# Revit family: TESK_Насос вертикальный_SVM(T)-45
name_source: partatom
category: Оборудование
units: mm (PartAtom-declared; Revit-internal decimal feet)

## family parameters
Всегда вертикально = Да
Классификация = Насос
На основе рабочей плоскости = Нет
Общий = Нет
При загрузке вырезать с полостями = Нет
Размер круглого соединителя = Использовать диаметр
Тип детали = Вставляется
Точка расчета площади = Нет

## types (50) — shared parameters
ADSK_Версия Revit = 2019
ADSK_Версия семейства = 1.0
ADSK_Диаметр условный = 80 мм
ADSK_Единица измерения = шт.
ADSK_Завод-изготовитель = TESK
ADSK_Классификация нагрузок = Прочее
ADSK_Количество = 1
ADSK_Количество фаз = 3
ADSK_Количество фаз числовое = 3
ADSK_Коэффициент мощности = 1
ADSK_Наименование краткое = Вертикальный многоступенчатый центробежный насос
ADSK_Напряжение = 400 В
URL = www.teskpump.ru
Материал_1 = TESK_Черный_Условный
Материал_2 = TESK_Нержавеющая сталь
Материал_КорпусДвигателя = TESK_Черный_Ребра_Условный
Таблица_Поиска = TESK_SVM(T)-45
УГО_Длина = 365 мм
Фланец_Толщина = 26 мм

## per-type parameters (varying)
| type | ADSK_Код изделия | ADSK_Масса | ADSK_Масса_Текст | ADSK_Наименование | ADSK_Номинальная мощность | ADSK_Полная мощность | D_Башня | Высота_Башня | Высота_Корпуса | Двигатель_Высота | Двигатель_ОтступКоробки | Двигатель_Ширина | Материал_КорпусУлитка | Напор максимальный | Толщина_ФланцаДвигателя |
| SVM 45-1-1 3kW 3x380V 50Hz IE3 | 7745-10-10003380NSSF | 89 | 89 | Вертикальный многоступенчатый центробежный насос SVM, DN80, PN25-40, Hmax=20м (3x380V 50Hz IE3) | 3 кВт | 3 кВ·А | 173 мм | 200 мм | 561 мм | 370 мм | 185 мм | 230 мм | TESK_Нержавеющая сталь | 20 | 11 мм |
| SVM 45-1 4kW 3x380V 50Hz IE3 | 7745-100003380NSSF | 89 | 89 | Вертикальный многоступенчатый центробежный насос SVM, DN80, PN25-40, Hmax=24м (3x380V 50Hz IE3) | 4 кВт | 4 кВ·А | 173 мм | 200 мм | 561 мм | 370 мм | 185 мм | 230 мм | TESK_Нержавеющая сталь | 24 | 11 мм |
| SVM 45-2-2 5.5kW 3x380V 50Hz IE3 | 7745-20-20003380NSSF | 108 | 108 | Вертикальный многоступенчатый центробежный насос SVM, DN80, PN25-40, Hmax=40м (3x380V 50Hz IE3) | 6 кВт | 6 кВ·А | 195 мм | 220 мм | 641 мм | 435 мм | 208 мм | 260 мм | TESK_Нержавеющая сталь | 40 | 13 мм |
| SVM 45-2 7.5kW 3x380V 50Hz IE3 | 7745-20  0003380NSSF | 108 | 108 | Вертикальный многоступенчатый центробежный насос SVM, DN80, PN25-40, Hmax=48м (3x380V 50Hz IE3) | 8 кВт | 8 кВ·А | 195 мм | 220 мм | 641 мм | 435 мм | 208 мм | 260 мм | TESK_Нержавеющая сталь | 48 | 13 мм |
| SVM 45-3-2 11kW 3x380V 50Hz IE3 | 7745-30-20003380NSSF | 183 | 183 | Вертикальный многоступенчатый центробежный насос SVM, DN80, PN25-40, Hmax=63м (3x380V 50Hz IE3) | 11 кВт | 11 кВ·А | 263 мм | 260 мм | 826 мм | 580 мм | 260 мм | 350 мм | TESK_Нержавеющая сталь | 63 | 17 мм |
| SVM 45-3 11kW 3x380V 50Hz IE3 | 7745-300003380NSSF | 183 | 183 | Вертикальный многоступенчатый центробежный насос SVM, DN80, PN25-40, Hmax=71м (3x380V 50Hz IE3) | 11 кВт | 11 кВ·А | 263 мм | 260 мм | 826 мм | 580 мм | 260 мм | 350 мм | TESK_Нержавеющая сталь | 71 | 17 мм |
| SVM 45-4-2 15kW 3x380V 50Hz IE3 | 7745-40-20003380NSSF | 197 | 197 | Вертикальный многоступенчатый центробежный насос SVM, DN80, PN25-40, Hmax=87м (3x380V 50Hz IE3) | 15 кВт | 15 кВ·А | 263 мм | 300 мм | 906 мм | 580 мм | 260 мм | 350 мм | TESK_Нержавеющая сталь | 87 | 17 мм |
| SVM 45-4 15kW 3x380V 50Hz IE3 | 7745-400003380NSSF | 197 | 197 | Вертикальный многоступенчатый центробежный насос SVM, DN80, PN25-40, Hmax=95м (3x380V 50Hz IE3) | 15 кВт | 15 кВ·А | 263 мм | 300 мм | 906 мм | 580 мм | 260 мм | 350 мм | TESK_Нержавеющая сталь | 95 | 17 мм |
| SVM 45-5-2 18.5kW 3x380V 50Hz IE3 | 7745-50-20003380NSSF | 221 | 221 | Вертикальный многоступенчатый центробежный насос SVM, DN80, PN25-40, Hmax=111м (3x380V 50Hz IE3) | 19 кВт | 19 кВ·А | 263 мм | 320 мм | 986 мм | 610 мм | 260 мм | 350 мм | TESK_Нержавеющая сталь | 111 | 18 мм |
| SVM 45-5 18.5kW 3x380V 50Hz IE3 | 7745-500003380NSSF | 221 | 221 | Вертикальный многоступенчатый центробежный насос SVM, DN80, PN25-40, Hmax=119м (3x380V 50Hz IE3) | 19 кВт | 19 кВ·А | 263 мм | 320 мм | 986 мм | 610 мм | 260 мм | 350 мм | TESK_Нержавеющая сталь | 119 | 18 мм |
| SVM 45-6-2 22kW 3x380V 50Hz IE3 | 7745-60-20003380NSSF | 261 | 261 | Вертикальный многоступенчатый центробежный насос SVM, DN80, PN25-40, Hmax=135м (3x380V 50Hz IE3) | 22 кВт | 22 кВ·А | 270 мм | 340 мм | 1066 мм | 645 мм | 285 мм | 360 мм | TESK_Нержавеющая сталь | 135 | 19 мм |
| SVM 45-6 22kW 3x380V 50Hz IE3 | 7745-60   0003380NSSF | 261 | 261 | Вертикальный многоступенчатый центробежный насос SVM, DN80, PN25-40, Hmax=143м (3x380V 50Hz IE3) | 22 кВт | 22 кВ·А | 270 мм | 340 мм | 1066 мм | 645 мм | 285 мм | 360 мм | TESK_Нержавеющая сталь | 143 | 19 мм |
| SVM 45-7-2 30kW 3x380V 50Hz IE3 | 7745-70-20003380NSSF | 320 | 320 | Вертикальный многоступенчатый центробежный насос SVM, DN80, PN25-40, Hmax=158м (3x380V 50Hz IE3) | 30 кВт | 30 кВ·А | 300 мм | 380 мм | 1146 мм | 705 мм | 310 мм | 400 мм | TESK_Нержавеющая сталь | 158 | 21 мм |
| SVM 45-7 30kW 3x380V 50Hz IE3 | 7745-700003380NSSF | 320 | 320 | Вертикальный многоступенчатый центробежный насос SVM, DN80, PN25-40, Hmax=166м (3x380V 50Hz IE3) | 30 кВт | 30 кВ·А | 300 мм | 380 мм | 1146 мм | 705 мм | 310 мм | 400 мм | TESK_Нержавеющая сталь | 166 | 21 мм |
| SVM 45-8-2 30kW 3x380V 50Hz IE3 | 7745-80-20003380NSSF | 324 | 324 | Вертикальный многоступенчатый центробежный насос SVM, DN80, PN25-40, Hmax=182м (3x380V 50Hz IE3) | 30 кВт | 30 кВ·А | 300 мм | 400 мм | 1226 мм | 705 мм | 310 мм | 400 мм | TESK_Нержавеющая сталь | 182 | 21 мм |
| SVM 45-8 30kW 3x380V 50Hz IE3 | 7745-80  0003380NSSF | 324 | 324 | Вертикальный многоступенчатый центробежный насос SVM, DN80, PN25-40, Hmax=190м (3x380V 50Hz IE3) | 30 кВт | 30 кВ·А | 300 мм | 400 мм | 1226 мм | 705 мм | 310 мм | 400 мм | TESK_Нержавеющая сталь | 190 | 21 мм |
| SVM 45-9-2 30kW 3x380V 50Hz IE3 | 7745-90-20003380NSSF | 340 | 340 | Вертикальный многоступенчатый центробежный насос SVM, DN80, PN25-40, Hmax=205м (3x380V 50Hz IE3) | 30 кВт | 30 кВ·А | 300 мм | 420 мм | 1306 мм | 705 мм | 310 мм | 400 мм | TESK_Нержавеющая сталь | 205 | 21 мм |
| SVM 45-9 37kW 3x380V 50Hz IE3 | 7745-90  0003380NSSF | 340 | 340 | Вертикальный многоступенчатый центробежный насос SVM, DN80, PN25-40, Hmax=214м (3x380V 50Hz IE3) | 37 кВт | 37 кВ·А | 300 мм | 420 мм | 1306 мм | 705 мм | 310 мм | 400 мм | TESK_Нержавеющая сталь | 214 | 21 мм |
| SVM 45-10-2 37kW 3x380V 50Hz IE3 | 7745-100-20003380NSSF | 355 | 355 | Вертикальный многоступенчатый центробежный насос SVM, DN80, PN25-40, Hmax=230м (3x380V 50Hz IE3) | 37 кВт | 37 кВ·А | 300 мм | 440 мм | 1386 мм | 705 мм | 310 мм | 400 мм | TESK_Нержавеющая сталь | 230 | 21 мм |
| SVM 45-10 37kW 3x380V 50Hz IE3 | 7745-100 0003380NSSF | 355 | 355 | Вертикальный многоступенчатый центробежный насос SVM, DN80, PN25-40, Hmax=238м (3x380V 50Hz IE3) | 37 кВт | 37 кВ·А | 300 мм | 440 мм | 1386 мм | 705 мм | 310 мм | 400 мм | TESK_Нержавеющая сталь | 238 | 21 мм |
| SVM 45-11-2 45kW 3x380V 50Hz IE3 | 7745-110-20003380NSSF | 426 | 426 | Вертикальный многоступенчатый центробежный насос SVM, DN80, PN25-40, Hmax=255м (3x380V 50Hz IE3) | 45 кВт | 45 кВ·А | 338 мм | 460 мм | 1466 мм | 740 мм | 345 мм | 450 мм | TESK_Нержавеющая сталь | 255 | 22 мм |
| SVM 45-11 45kW 3x380V 50Hz IE3 | 7745-110 0003380NSSF | 426 | 426 | Вертикальный многоступенчатый центробежный насос SVM, DN80, PN25-40, Hmax=263м (3x380V 50Hz IE3) | 45 кВт | 45 кВ·А | 338 мм | 460 мм | 1466 мм | 740 мм | 345 мм | 450 мм | TESK_Нержавеющая сталь | 263 | 22 мм |
| SVM 45-12-2 45kW 3x380V 50Hz IE3 | 7745-120-20003380NSSF | 432 | 432 | Вертикальный многоступенчатый центробежный насос SVM, DN80, PN25-40, Hmax=280м (3x380V 50Hz IE3) | 45 кВт | 45 кВ·А | 338 мм | 480 мм | 1546 мм | 740 мм | 345 мм | 450 мм | TESK_Нержавеющая сталь | 280 | 22 мм |
| SVM 45-12 45kW 3x380V 50Hz IE3 | 7745-130-20003380NSSF | 432 | 432 | Вертикальный многоступенчатый центробежный насос SVM, DN80, PN25-40, Hmax=289м (3x380V 50Hz IE3) | 45 кВт | 45 кВ·А | 338 мм | 480 мм | 1546 мм | 740 мм | 345 мм | 450 мм | TESK_Нержавеющая сталь | 289 | 22 мм |
| SVM 45-13-2 45kW 3x380V 50Hz IE3 | 7745-120 0003380NSSF | 438 | 438 | Вертикальный многоступенчатый центробежный насос SVM, DN80, PN25-40, Hmax=305м (3x380V 50Hz IE3) | 45 кВт | 45 кВ·А | 338 мм | 500 мм | 1626 мм | 740 мм | 345 мм | 450 мм | TESK_Нержавеющая сталь | 305 | 22 мм |
| SVMT 45-1-1 3kW 3x380V 50Hz IE3 | 7745-10-10003380N | 89 | 89 | Вертикальный многоступенчатый центробежный насос SVMT, DN80, PN25-40, Hmax=20м (3x380V 50Hz IE3) | 3 кВт | 3 кВ·А | 173 мм | 200 мм | 561 мм | 370 мм | 185 мм | 230 мм | TESK_Черный_Условный | 20 | 11 мм |
| SVMT 45-1 4kW 3x380V 50Hz IE3 | 7745-100003380N | 89 | 89 | Вертикальный многоступенчатый центробежный насос SVMT, DN80, PN25-40, Hmax=24м (3x380V 50Hz IE3) | 4 кВт | 4 кВ·А | 173 мм | 200 мм | 561 мм | 370 мм | 185 мм | 230 мм | TESK_Черный_Условный | 24 | 11 мм |
| SVMT 45-2-2 5.5kW 3x380V 50Hz IE3 | 7745-20-20003380N | 108 | 108 | Вертикальный многоступенчатый центробежный насос SVMT, DN80, PN25-40, Hmax=40м (3x380V 50Hz IE3) | 6 кВт | 6 кВ·А | 195 мм | 220 мм | 641 мм | 435 мм | 208 мм | 260 мм | TESK_Черный_Условный | 40 | 13 мм |
| SVMT 45-2 7.5kW 3x380V 50Hz IE3 | 7745-20  0003380N | 108 | 108 | Вертикальный многоступенчатый центробежный насос SVMT, DN80, PN25-40, Hmax=48м (3x380V 50Hz IE3) | 8 кВт | 8 кВ·А | 195 мм | 220 мм | 641 мм | 435 мм | 208 мм | 260 мм | TESK_Черный_Условный | 48 | 13 мм |
| SVMT 45-3-2 11kW 3x380V 50Hz IE3 | 7745-30-20003380N | 183 | 183 | Вертикальный многоступенчатый центробежный насос SVMT, DN80, PN25-40, Hmax=63м (3x380V 50Hz IE3) | 11 кВт | 11 кВ·А | 263 мм | 260 мм | 826 мм | 580 мм | 260 мм | 350 мм | TESK_Черный_Условный | 63 | 17 мм |
| SVMT 45-3 11kW 3x380V 50Hz IE3 | 7745-300003380N | 183 | 183 | Вертикальный многоступенчатый центробежный насос SVMT, DN80, PN25-40, Hmax=71м (3x380V 50Hz IE3) | 11 кВт | 11 кВ·А | 263 мм | 260 мм | 826 мм | 580 мм | 260 мм | 350 мм | TESK_Черный_Условный | 71 | 17 мм |
| SVMT 45-4-2 15kW 3x380V 50Hz IE3 | 7745-40-20003380N | 197 | 197 | Вертикальный многоступенчатый центробежный насос SVMT, DN80, PN25-40, Hmax=87м (3x380V 50Hz IE3) | 15 кВт | 15 кВ·А | 263 мм | 300 мм | 906 мм | 580 мм | 260 мм | 350 мм | TESK_Черный_Условный | 87 | 17 мм |
| SVMT 45-4 15kW 3x380V 50Hz IE3 | 7745-400003380N | 197 | 197 | Вертикальный многоступенчатый центробежный насос SVMT, DN80, PN25-40, Hmax=95м (3x380V 50Hz IE3) | 15 кВт | 15 кВ·А | 263 мм | 300 мм | 906 мм | 580 мм | 260 мм | 350 мм | TESK_Черный_Условный | 95 | 17 мм |
| SVMT 45-5-2 18.5kW 3x380V 50Hz IE3 | 7745-50-20003380N | 221 | 221 | Вертикальный многоступенчатый центробежный насос SVMT, DN80, PN25-40, Hmax=111м (3x380V 50Hz IE3) | 19 кВт | 19 кВ·А | 263 мм | 320 мм | 986 мм | 610 мм | 260 мм | 350 мм | TESK_Черный_Условный | 111 | 18 мм |
| SVMT 45-5 18.5kW 3x380V 50Hz IE3 | 7745-500003380N | 221 | 221 | Вертикальный многоступенчатый центробежный насос SVMT, DN80, PN25-40, Hmax=119м (3x380V 50Hz IE3) | 19 кВт | 19 кВ·А | 263 мм | 320 мм | 986 мм | 610 мм | 260 мм | 350 мм | TESK_Черный_Условный | 119 | 18 мм |
| SVMT 45-6-2 22kW 3x380V 50Hz IE3 | 7745-60-20003380N | 261 | 261 | Вертикальный многоступенчатый центробежный насос SVMT, DN80, PN25-40, Hmax=135м (3x380V 50Hz IE3) | 22 кВт | 22 кВ·А | 270 мм | 340 мм | 1066 мм | 645 мм | 285 мм | 360 мм | TESK_Черный_Условный | 135 | 19 мм |
| SVMT 45-6 22kW 3x380V 50Hz IE3 | 7745-60   0003380N | 261 | 261 | Вертикальный многоступенчатый центробежный насос SVMT, DN80, PN25-40, Hmax=143м (3x380V 50Hz IE3) | 22 кВт | 22 кВ·А | 270 мм | 340 мм | 1066 мм | 645 мм | 285 мм | 360 мм | TESK_Черный_Условный | 143 | 19 мм |
| SVMT 45-7-2 30kW 3x380V 50Hz IE3 | 7745-70-20003380N | 320 | 320 | Вертикальный многоступенчатый центробежный насос SVMT, DN80, PN25-40, Hmax=158м (3x380V 50Hz IE3) | 30 кВт | 30 кВ·А | 300 мм | 380 мм | 1146 мм | 705 мм | 310 мм | 400 мм | TESK_Черный_Условный | 158 | 21 мм |
| SVMT 45-7 30kW 3x380V 50Hz IE3 | 7745-700003380N | 320 | 320 | Вертикальный многоступенчатый центробежный насос SVMT, DN80, PN25-40, Hmax=166м (3x380V 50Hz IE3) | 30 кВт | 30 кВ·А | 300 мм | 380 мм | 1146 мм | 705 мм | 310 мм | 400 мм | TESK_Черный_Условный | 166 | 21 мм |
| SVMT 45-8-2 30kW 3x380V 50Hz IE3 | 7745-80-20003380N | 324 | 324 | Вертикальный многоступенчатый центробежный насос SVMT, DN80, PN25-40, Hmax=182м (3x380V 50Hz IE3) | 30 кВт | 30 кВ·А | 300 мм | 400 мм | 1226 мм | 705 мм | 310 мм | 400 мм | TESK_Черный_Условный | 182 | 21 мм |
| SVMT 45-8 30kW 3x380V 50Hz IE3 | 7745-80  0003380N | 324 | 324 | Вертикальный многоступенчатый центробежный насос SVMT, DN80, PN25-40, Hmax=190м (3x380V 50Hz IE3) | 30 кВт | 30 кВ·А | 300 мм | 400 мм | 1226 мм | 705 мм | 310 мм | 400 мм | TESK_Черный_Условный | 190 | 21 мм |
| SVMT 45-9-2 30kW 3x380V 50Hz IE3 | 7745-90-20003380N | 340 | 340 | Вертикальный многоступенчатый центробежный насос SVMT, DN80, PN25-40, Hmax=205м (3x380V 50Hz IE3) | 30 кВт | 30 кВ·А | 300 мм | 420 мм | 1306 мм | 705 мм | 310 мм | 400 мм | TESK_Черный_Условный | 205 | 21 мм |
| SVMT 45-9 37kW 3x380V 50Hz IE3 | 7745-90  0003380N | 340 | 340 | Вертикальный многоступенчатый центробежный насос SVMT, DN80, PN25-40, Hmax=214м (3x380V 50Hz IE3) | 37 кВт | 37 кВ·А | 300 мм | 420 мм | 1306 мм | 705 мм | 310 мм | 400 мм | TESK_Черный_Условный | 214 | 21 мм |
| SVMT 45-10-2 37kW 3x380V 50Hz IE3 | 7745-100-20003380N | 355 | 355 | Вертикальный многоступенчатый центробежный насос SVMT, DN80, PN25-40, Hmax=230м (3x380V 50Hz IE3) | 37 кВт | 37 кВ·А | 300 мм | 440 мм | 1386 мм | 705 мм | 310 мм | 400 мм | TESK_Черный_Условный | 230 | 21 мм |
| SVMT 45-10 37kW 3x380V 50Hz IE3 | 7745-100 0003380N | 355 | 355 | Вертикальный многоступенчатый центробежный насос SVMT, DN80, PN25-40, Hmax=238м (3x380V 50Hz IE3) | 37 кВт | 37 кВ·А | 300 мм | 440 мм | 1386 мм | 705 мм | 310 мм | 400 мм | TESK_Черный_Условный | 238 | 21 мм |
| SVMT 45-11-2 45kW 3x380V 50Hz IE3 | 7745-110-20003380N | 426 | 426 | Вертикальный многоступенчатый центробежный насос SVMT, DN80, PN25-40, Hmax=255м (3x380V 50Hz IE3) | 45 кВт | 45 кВ·А | 338 мм | 460 мм | 1466 мм | 740 мм | 345 мм | 450 мм | TESK_Черный_Условный | 255 | 22 мм |
| SVMT 45-11 45kW 3x380V 50Hz IE3 | 7745-110 0003380N | 426 | 426 | Вертикальный многоступенчатый центробежный насос SVMT, DN80, PN25-40, Hmax=263м (3x380V 50Hz IE3) | 45 кВт | 45 кВ·А | 338 мм | 460 мм | 1466 мм | 740 мм | 345 мм | 450 мм | TESK_Черный_Условный | 263 | 22 мм |
| SVMT 45-12-2 45kW 3x380V 50Hz IE3 | 7745-120-20003380N | 432 | 432 | Вертикальный многоступенчатый центробежный насос SVMT, DN80, PN25-40, Hmax=280м (3x380V 50Hz IE3) | 45 кВт | 45 кВ·А | 338 мм | 480 мм | 1546 мм | 740 мм | 345 мм | 450 мм | TESK_Черный_Условный | 280 | 22 мм |
| SVMT 45-12 45kW 3x380V 50Hz IE3 | 7745-130-20003380N | 432 | 432 | Вертикальный многоступенчатый центробежный насос SVMT, DN80, PN25-40, Hmax=289м (3x380V 50Hz IE3) | 45 кВт | 45 кВ·А | 338 мм | 480 мм | 1546 мм | 740 мм | 345 мм | 450 мм | TESK_Черный_Условный | 289 | 22 мм |
| SVMT 45-13-2 45kW 3x380V 50Hz IE3 | 7745-120 0003380N | 438 | 438 | Вертикальный многоступенчатый центробежный насос SVMT, DN80, PN25-40, Hmax=305м (3x380V 50Hz IE3) | 45 кВт | 45 кВ·А | 338 мм | 500 мм | 1626 мм | 740 мм | 345 мм | 450 мм | TESK_Черный_Условный | 305 | 22 мм |

note: column(s) folded — value = type name in every type: ADSK_Марка
